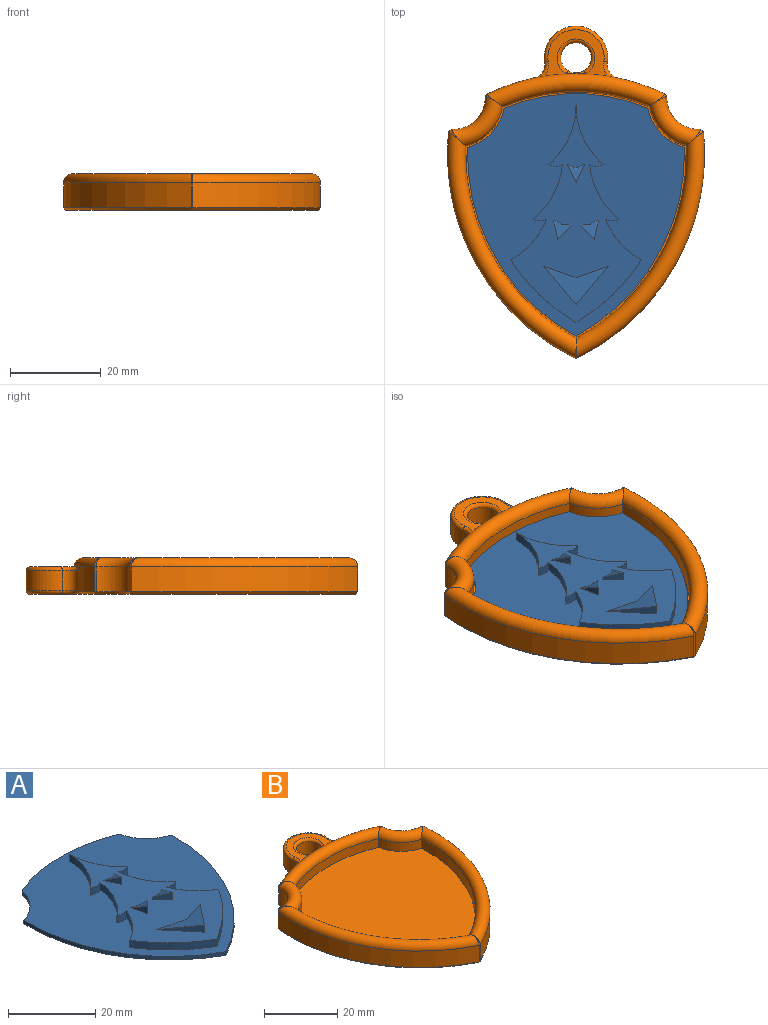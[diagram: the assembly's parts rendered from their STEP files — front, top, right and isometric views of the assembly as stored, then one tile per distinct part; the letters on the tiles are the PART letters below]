
ASSEMBLY  parts=2 mates=1
PART A: 40 faces, bbox 47.8x53.3x5 mm
  f0: plane 53.35x47.8mm, normal (0,0,1), area 1241.3mm2, adj f1,f2,f3,f4,f5,f7,f8,f9
  f1: cylinder r=11.4mm len=8.63mm, axis (0,0,-1), area 12.4mm2, adj f0,f2,f5,f6
  f2: cylinder r=45.6mm len=41.51mm, axis (0,0,-1), area 50.4mm2, adj f0,f1,f3,f6
  f3: cylinder r=45.6mm len=41.51mm, axis (0,0,-1), area 50.4mm2, adj f0,f2,f4,f6
  f4: cylinder r=11.4mm len=8.63mm, axis (0,0,-1), area 12.4mm2, adj f0,f3,f5,f6
  f5: cylinder r=40.6mm len=31.64mm, axis (0,0,-1), area 32.5mm2, adj f0,f1,f4,f6
  f6: plane 53.35x47.8mm, normal (0,0,-1), area 1816.2mm2, adj f1,f2,f3,f4,f5
  f7: cylinder r=43mm len=14.4mm, axis (0,0,-1), area 40.2mm2, adj f0,f8,f18,f19
  f8: cylinder r=17.08mm len=9mm, axis (0,0,-1), area 24.5mm2, adj f0,f7,f9,f19
  f9: cylinder r=3mm len=3mm, axis (0,0,-1), area 6.3mm2, adj f0,f8,f10,f19
  f10: cylinder r=17.08mm len=12mm, axis (0,0,-1), area 28.1mm2, adj f0,f9,f11,f19
  f11: cylinder r=3mm len=3mm, axis (0,0,-1), area 6.3mm2, adj f0,f10,f12,f19
  f12: cylinder r=17.08mm len=13mm, axis (0,0,-1), area 29.5mm2, adj f0,f11,f13,f19
  f13: cylinder r=17.08mm len=13mm, axis (0,0,-1), area 29.5mm2, adj f0,f12,f14,f19
  f14: cylinder r=3mm len=3mm, axis (0,0,-1), area 6.3mm2, adj f0,f13,f15,f19
  f15: cylinder r=17.08mm len=12mm, axis (0,0,-1), area 28.1mm2, adj f0,f14,f16,f19
  f16: cylinder r=3mm len=3mm, axis (0,0,-1), area 6.3mm2, adj f0,f15,f17,f19
  f17: cylinder r=17.08mm len=9mm, axis (0,0,-1), area 24.5mm2, adj f0,f16,f18,f19
  f18: cylinder r=43mm len=14.4mm, axis (0,0,-1), area 40.2mm2, adj f0,f7,f17,f19
  f19: plane 47.77x28.8mm, normal (0,0,1), area 512.9mm2, adj f7,f8,f9,f10,f11,f12,f13,f14
  f20: plane 4x2mm, normal (0.91,-0.42,0), area 4.4mm2, adj f19,f23,f39
  f21: plane 1.87x0.68mm, normal (-0.34,0.94,0), area 0.3mm2, adj f19,f22,f39
  f22: plane 1.87x0.68mm, normal (0.34,0.94,0), area 0.3mm2, adj f19,f21,f39
  f23: plane 4x2mm, normal (-0.91,-0.42,0), area 4.4mm2, adj f19,f20,f39
  f24: plane 4.5x2mm, normal (-0.98,-0.22,0), area 4.6mm2, adj f19,f25,f38
  f25: plane 3.4x3.11mm, normal (0.74,-0.68,0), area 5.7mm2, adj f19,f24,f26,f38
  f26: plane 2.23x0.53mm, normal (-0.04,1,0), area 1.1mm2, adj f19,f25,f27,f38
  f27: plane 1.88x1.2mm, normal (0.54,0.84,0), area 0.6mm2, adj f19,f26,f38
  f28: plane 8.43x7.07mm, normal (0.77,-0.64,0), area 11mm2, adj f19,f31,f37
  f29: plane 7.07x2.57mm, normal (-0.34,0.94,0), area 2.3mm2, adj f19,f30,f37
  f30: plane 7.07x2.57mm, normal (0.34,0.94,0), area 2.3mm2, adj f19,f29,f37
  f31: plane 8.43x7.07mm, normal (-0.77,-0.64,0), area 11mm2, adj f19,f28,f37
  f32: plane 3.4x3.11mm, normal (-0.74,-0.68,0), area 5.7mm2, adj f19,f33,f35,f36
  f33: plane 4.5x2mm, normal (0.98,-0.22,0), area 4.6mm2, adj f19,f32,f36
  f34: plane 1.88x1.2mm, normal (-0.54,0.84,0), area 0.6mm2, adj f19,f35,f36
  f35: plane 2.23x0.53mm, normal (0.04,1,0), area 1.1mm2, adj f19,f32,f34,f36
  f36: plane 4.5x4.11mm, normal (0,0.41,0.91), area 8mm2, adj f32,f33,f34,f35
  f37: plane 14.14x8.43mm, normal (0,0.23,0.97), area 42.5mm2, adj f28,f29,f30,f31
  f38: plane 4.5x4.11mm, normal (0,0.41,0.91), area 8mm2, adj f24,f25,f26,f27
  f39: plane 4x3.73mm, normal (0,0.45,0.89), area 6.9mm2, adj f20,f21,f22,f23
PART B: 55 faces, bbox 64.8x77.4x8 mm
  f0: cylinder r=45mm len=10.44mm, axis (0,0,-1), area 59.7mm2, adj f13,f18,f27,f33,f36,f37
  f1: cylinder r=45mm len=10.44mm, axis (0,0,-1), area 59.7mm2, adj f13,f20,f29,f34,f38,f39
  f2: cylinder r=7mm len=7.54mm, axis (0,0,-1), area 64.9mm2, adj f12,f39,f46,f47
  f3: cylinder r=50mm len=49.89mm, axis (0,0,-1), area 334.4mm2, adj f14,f47,f51,f53
  f4: cylinder r=50mm len=49.89mm, axis (0,0,-1), area 334.4mm2, adj f16,f44,f50,f53
  f5: cylinder r=46mm len=42.28mm, axis (0,0,-1), area 154.1mm2, adj f6,f9,f14,f17
  f6: cylinder r=11mm len=8.6mm, axis (0,0,-1), area 37.4mm2, adj f5,f7,f12,f17
  f7: cylinder r=41mm len=32.34mm, axis (0,0,-1), area 99.7mm2, adj f6,f8,f13,f17
  f8: cylinder r=11mm len=8.6mm, axis (0,0,-1), area 37.4mm2, adj f7,f9,f15,f17
  f9: cylinder r=46mm len=42.28mm, axis (0,0,-1), area 154.1mm2, adj f5,f8,f16,f17
  f10: cylinder r=7mm len=7.54mm, axis (0,0,-1), area 64.9mm2, adj f15,f36,f44,f45
  f11: plane 71.83x55.6mm, normal (0,0,-1), area 2545mm2, adj f23,f24,f25,f26,f37,f38,f45,f46
  f12: torus R=9mm, axis (0,0,1), area 78.2mm2, adj f2,f6,f13,f14,f35,f43
  f13: torus R=43mm, axis (0,0,1), area 235.1mm2, adj f0,f1,f7,f12,f15,f22,f27,f29
  f14: torus R=48mm, axis (0,0,1), area 353mm2, adj f3,f5,f12,f16,f43,f54
  f15: torus R=9mm, axis (0,0,1), area 78.2mm2, adj f8,f10,f13,f16,f32,f40
  f16: torus R=48mm, axis (0,0,1), area 353mm2, adj f4,f9,f14,f15,f40,f54
  f17: plane 54.2x48.6mm, normal (0,0,1), area 1880mm2, adj f5,f6,f7,f8,f9
  f18: cylinder r=3mm len=4.4mm, axis (0,0,-1), area 20.6mm2, adj f0,f19,f23,f27
  f19: cylinder r=7mm len=14mm, axis (0,0,-1), area 105.1mm2, adj f18,f20,f24,f28
  f20: cylinder r=3mm len=4.4mm, axis (0,0,-1), area 20.6mm2, adj f1,f19,f25,f29
  f21: cylinder r=3.35mm len=6.7mm, axis (0,0,-1), area 92.6mm2, adj f26,f30,f31
  f22: plane 14.08x10.25mm, normal (0,0,1), area 54mm2, adj f13,f27,f28,f29,f30
  f23: torus R=3.8mm, axis (0,0,1), area 7.3mm2, adj f11,f18,f24,f33
  f24: torus R=6.2mm, axis (0,0,1), area 28.7mm2, adj f11,f19,f23,f25
  f25: torus R=3.8mm, axis (0,0,1), area 7.3mm2, adj f11,f20,f24,f34
  f26: torus R=4.15mm, axis (0,0,1), area 28.7mm2, adj f11,f21
  f27: torus R=3.8mm, axis (0,0,1), area 5.1mm2, adj f0,f13,f18,f22,f28
  f28: torus R=6.2mm, axis (0,0,1), area 28.7mm2, adj f19,f22,f27,f29
  f29: torus R=3.8mm, axis (0,0,1), area 5.1mm2, adj f1,f13,f20,f22,f28
  f30: torus R=4.15mm, axis (0,0,1), area 23.8mm2, adj f21,f22,f31
  f31: bspline ~4.29x0.8mm, area 2.9mm2, adj f13,f21,f30
  f32: bspline ~2x1.98mm, area 0.7mm2, adj f13,f15,f36
  f33: bspline ~1.41x0.81mm, area 0.4mm2, adj f0,f23,f37
  f34: bspline ~1.41x0.81mm, area 0.4mm2, adj f1,f25,f38
  f35: bspline ~2x1.98mm, area 0.7mm2, adj f12,f13,f39
  f36: plane 5.5x0.47mm, normal (0.86,0.51,0), area 3mm2, adj f0,f10,f32,f41
  f37: cone r=45mm half-angle=45deg, axis (0,0,1), area 6.8mm2, adj f0,f11,f33,f41
  f38: cone r=45mm half-angle=45deg, axis (0,0,1), area 6.8mm2, adj f1,f11,f34,f42
  f39: plane 5.5x0.47mm, normal (-0.86,0.51,0), area 3mm2, adj f1,f2,f35,f42
  f40: bspline ~2.01x2mm, area 1mm2, adj f15,f16,f44
  f41: plane 0.5x0.5mm, normal (0.66,0.39,-0.64), area 0.2mm2, adj f36,f37,f45
  f42: plane 0.5x0.5mm, normal (-0.66,0.39,-0.64), area 0.2mm2, adj f38,f39,f46
  f43: bspline ~2.01x2mm, area 1mm2, adj f12,f14,f47
  f44: plane 5.5x0.54mm, normal (0.64,0.77,0), area 3.8mm2, adj f4,f10,f40,f48
  f45: cone r=7.5mm half-angle=45deg, axis (0,0,-1), area 8.6mm2, adj f10,f11,f41,f48
  f46: cone r=7.5mm half-angle=45deg, axis (0,0,-1), area 8.6mm2, adj f2,f11,f42,f49
  f47: plane 5.5x0.54mm, normal (-0.64,0.77,0), area 3.8mm2, adj f2,f3,f43,f49
  f48: plane 0.54x0.5mm, normal (0.52,0.62,-0.58), area 0.2mm2, adj f44,f45,f50
  f49: plane 0.54x0.5mm, normal (-0.52,0.62,-0.58), area 0.2mm2, adj f46,f47,f51
  f50: cone r=50mm half-angle=45deg, axis (0,0,1), area 42.8mm2, adj f4,f11,f48,f52
  f51: cone r=50mm half-angle=45deg, axis (0,0,1), area 42.8mm2, adj f3,f11,f49,f52
  f52: plane 0.5x0.45mm, normal (0,-0.74,-0.67), area 0.1mm2, adj f50,f51,f53
  f53: plane 5.5x0.44mm, normal (0,-1,0), area 2.4mm2, adj f3,f4,f52,f54
  f54: bspline ~2.13x2mm, area 0.6mm2, adj f14,f16,f53
PLACE A t=(0,0,3)mm
PLACE B at identity fixed
MATE fastened B.f17 <-> A.f6  axis (0,0,1) through (0,-1.73,3)mm
